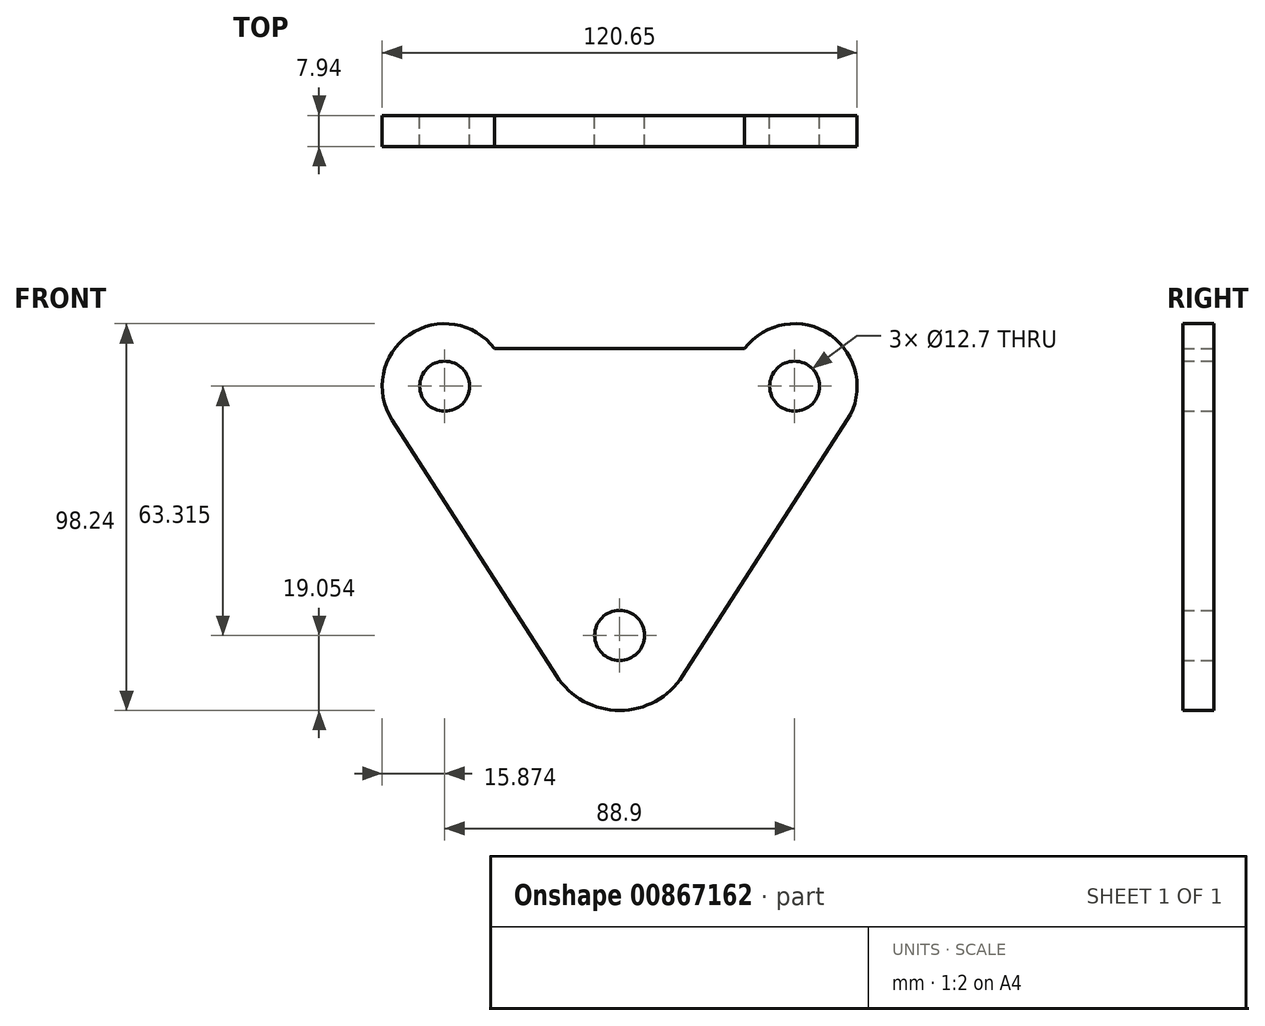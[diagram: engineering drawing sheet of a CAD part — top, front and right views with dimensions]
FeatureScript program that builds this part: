
annotation { "Feature Type Name" : "Feature", "Feature Type Description" : "" }
export const myFeature = defineFeature(function(context is Context, id is Id, definition is map)
    precondition{}
    {
        {
            var Q0;
            Q0=qCreatedBy(makeId("Front.planeOp"),FACE);
            var sketch = newSketch(context, id + "F0", { "sketchPlane" : qUnion([Q0])});
            skCircle(sketch, "E0", {"center": v(-47.4, 47.35) * mm, "radius": 6.35 * mm});
            skCircle(sketch, "E1", {"center": v(41.5, 47.35) * mm, "radius": 6.35 * mm});
            skCircle(sketch, "E2", {"center": v(-2.95, -15.97) * mm, "radius": 6.35 * mm});
            skArc(sketch, "E3", {"start": v(-34.7, 56.87) * mm, "mid": v(-56.45, 60.39) * mm, "end": v(-60.75, 38.77) * mm});
            skArc(sketch, "E4", {"start": v(54.86, 38.77) * mm, "mid": v(50.56, 60.39) * mm, "end": v(28.8, 56.87) * mm});
            skArc(sketch, "E5", {"start": v(-18.97, -26.26) * mm, "mid": v(-2.95, -35.02) * mm, "end": v(13.08, -26.26) * mm});
            skLineSegment(sketch, "E6", {"start": v(-60.75, 38.77) * mm, "end": v(-18.97, -26.26) * mm});
            skLineSegment(sketch, "E7", {"start": v(13.08, -26.26) * mm, "end": v(54.86, 38.77) * mm});
            skLineSegment(sketch, "E8", {"start": v(-34.7, 56.87) * mm, "end": v(28.8, 56.87) * mm});
            skSolve(sketch);
        }
        {
            var Q0;
            Q0=makeQuery(id+"F0.imprint","IMPRINT",FACE,{"disambiguationData":[TD([[makeQuery(id+"F0.imprint","IMPRINT",EDGE,{"derivedFrom":sQuery(id+"F0.wireOp",EDGE,"E0")}),-1.0]])]});
            extrude(context, id + "F1", {"entities" : qUnion([Q0]), "depth" : 7.94 * mm, "offsetDistance" : 25.4 * mm});
        }
    });
